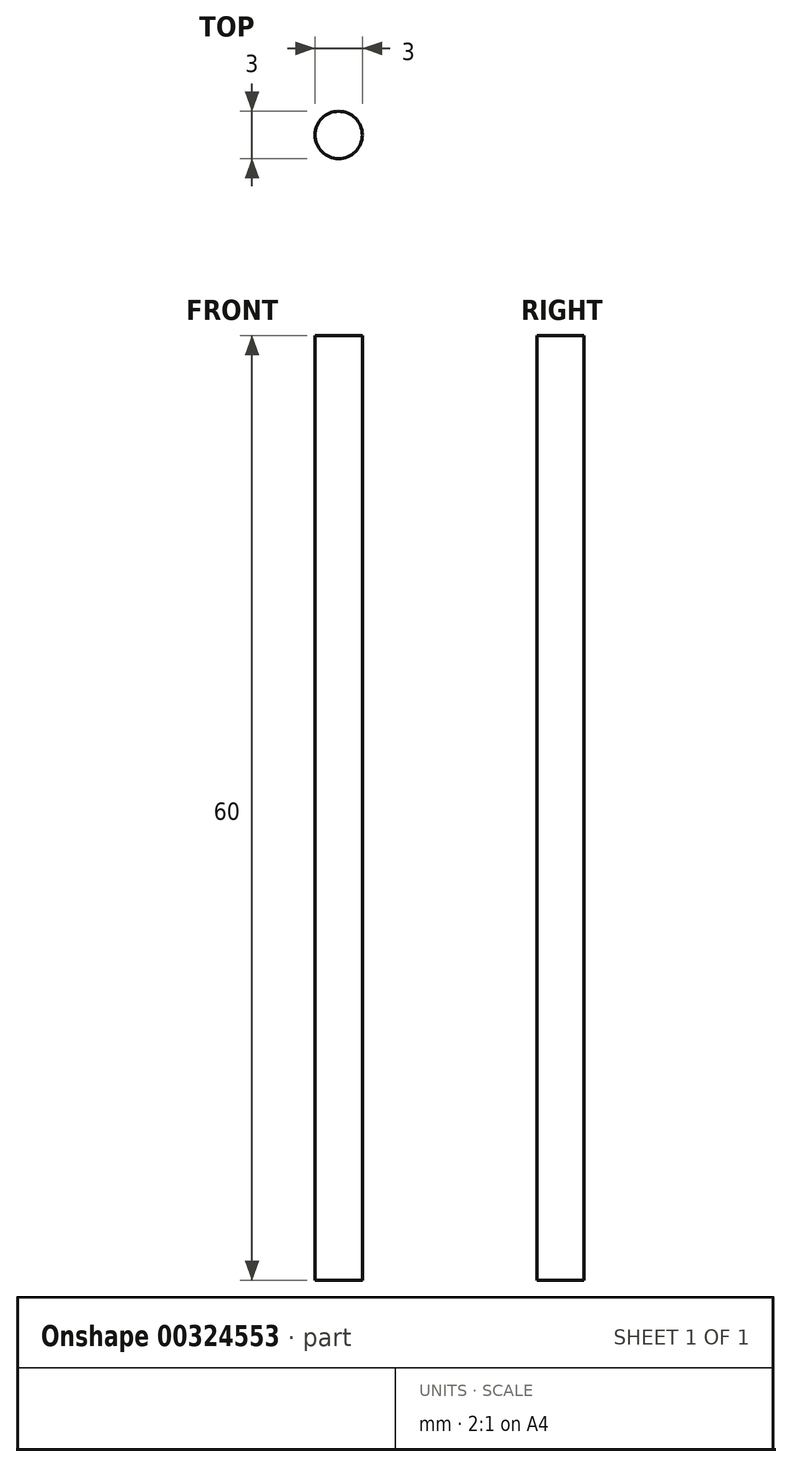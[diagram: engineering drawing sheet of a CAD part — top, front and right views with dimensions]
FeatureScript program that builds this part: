
annotation { "Feature Type Name" : "Feature", "Feature Type Description" : "" }
export const myFeature = defineFeature(function(context is Context, id is Id, definition is map)
    precondition{}
    {
        {
            var Q0;
            Q0=qCreatedBy(makeId("Top.planeOp"),FACE);
            var sketch = newSketch(context, id + "F0", { "sketchPlane" : qUnion([Q0])});
            skCircle(sketch, "E0", {"center": v(0, 0) * mm, "radius": 1.5 * mm});
            skSolve(sketch);
        }
        {
            var Q0;
            Q0=makeQuery(id+"F0.imprint","IMPRINT",FACE,{"disambiguationData":[TD([[makeQuery(id+"F0.imprint","IMPRINT",EDGE,{"derivedFrom":sQuery(id+"F0.wireOp",EDGE,"E0")}),1.0]])]});
            extrude(context, id + "F1", {"entities" : qUnion([Q0]), "depth" : 60 * mm});
        }
    });
